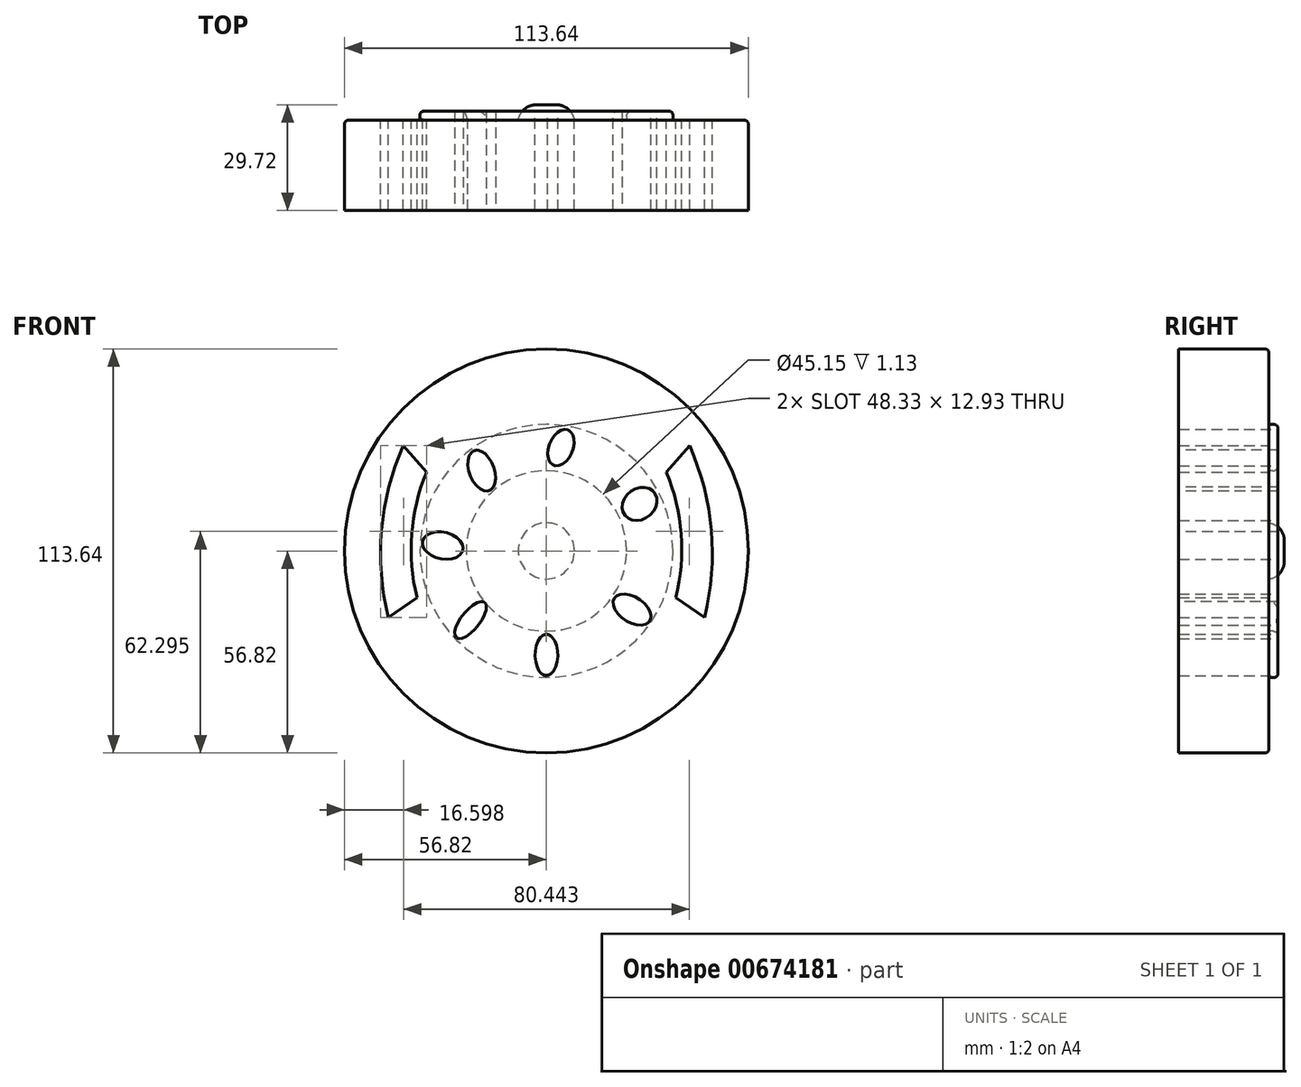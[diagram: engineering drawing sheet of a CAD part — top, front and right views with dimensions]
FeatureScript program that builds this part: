
annotation { "Feature Type Name" : "Feature", "Feature Type Description" : "" }
export const myFeature = defineFeature(function(context is Context, id is Id, definition is map)
    precondition{}
    {
        {
            var Q0;
            Q0=qCreatedBy(makeId("Front.planeOp"),FACE);
            var sketch = newSketch(context, id + "F0", { "sketchPlane" : qUnion([Q0])});
            skCircle(sketch, "E0", {"center": v(0, 0) * mm, "radius": 56.82 * mm});
            skSolve(sketch);
        }
        {
            var Q0;
            Q0=makeQuery(id+"F0.imprint","IMPRINT",FACE,{"disambiguationData":[TD([[makeQuery(id+"F0.imprint","IMPRINT",EDGE,{"derivedFrom":sQuery(id+"F0.wireOp",EDGE,"E0")}),1.0]])]});
            var sketch = newSketch(context, id + "F1", { "sketchPlane" : qUnion([Q0])});
            skLineSegment(sketch, "E1", {"start": v(0, 72.6) * mm, "end": v(0, -72.88) * mm, "construction": true});
            skLineSegment(sketch, "E2", {"start": v(-75.95, 0) * mm, "end": v(77.07, 0) * mm, "construction": true});
            skLineSegment(sketch, "E3", {"start": v(-40.28, 29.64) * mm, "end": v(-33.76, 22.16) * mm});
            skLineSegment(sketch, "E4", {"start": v(-44.47, -18.7) * mm, "end": v(-36.41, -13.13) * mm});
            skArc(sketch, "E5", {"start": v(-40.28, 29.64) * mm, "mid": v(-46.4, 5.82) * mm, "end": v(-44.47, -18.7) * mm});
            skArc(sketch, "E6", {"start": v(-33.76, 22.16) * mm, "mid": v(-37.9, 4.73) * mm, "end": v(-36.41, -13.13) * mm});
            skArc(sketch, "E7.MirrorCS", {"start": v(33.76, 22.16) * mm, "mid": v(37.9, 4.73) * mm, "end": v(36.41, -13.13) * mm});
            skLineSegment(sketch, "E8.MirrorCS", {"start": v(40.28, 29.64) * mm, "end": v(33.76, 22.16) * mm});
            skArc(sketch, "E9.MirrorCS", {"start": v(40.28, 29.64) * mm, "mid": v(46.4, 5.82) * mm, "end": v(44.47, -18.7) * mm});
            skLineSegment(sketch, "E10.MirrorCS", {"start": v(44.47, -18.7) * mm, "end": v(36.41, -13.13) * mm});
            skSolve(sketch);
        }
        {
            var Q0;
            Q0=makeQuery(id+"F1.imprint","IMPRINT",FACE,{"disambiguationData":[TD([[makeQuery(id+"F1.imprint","IMPRINT",EDGE,{"derivedFrom":sQuery(id+"F1.wireOp",EDGE,"E3")}),1.0]])]});
            extrude(context, id + "F2", {"entities" : qUnion([Q0]), "depth" : 25.4 * mm, "offsetDistance" : 25.4 * mm});
        }
        {
            var Q0;
            Q0=makeQuery(id+"F0.imprint","IMPRINT",FACE,{"disambiguationData":[TD([[makeQuery(id+"F0.imprint","IMPRINT",EDGE,{"derivedFrom":sQuery(id+"F0.wireOp",EDGE,"E0")}),1.0]])]});
            var sketch = newSketch(context, id + "F3", { "sketchPlane" : qUnion([Q0])});
            skCircle(sketch, "E11", {"center": v(0, 0) * mm, "radius": 35.59 * mm});
            skCircle(sketch, "E12", {"center": v(0, 0) * mm, "radius": 22.58 * mm});
            skSolve(sketch);
        }
        {
            var Q0;
            Q0 = qSketchRegion(id + "F3", true);
            var Q1;
            Q1=makeQuery(id+"F2.opExtrude","CAP_FACE",FACE,{"disambiguationData":[OSD([sQuery(id+"F0.wireOp",EDGE,"E0"),sQuery(id+"F1.wireOp",EDGE,"E3"),sQuery(id+"F1.wireOp",EDGE,"E4"),sQuery(id+"F1.wireOp",EDGE,"E5"),sQuery(id+"F1.wireOp",EDGE,"E6"),sQuery(id+"F1.wireOp",EDGE,"E7.MirrorCS"),sQuery(id+"F1.wireOp",EDGE,"E8.MirrorCS"),sQuery(id+"F1.wireOp",EDGE,"E9.MirrorCS"),sQuery(id+"F1.wireOp",EDGE,"E10.MirrorCS")])],"isStart":false});
            extrude(context, id + "F4", {"entities" : qUnion([Q0, Q1]), "operationType" : NewBodyOperationType.ADD, "oppositeDirection" : true, "depth" : 2.54 * mm, "offsetDistance" : 25.4 * mm});
        }
        {
            var Q0;
            Q0=makeQuery(id+"F4.opExtrude","CAP_FACE",FACE,{"disambiguationData":[OSD([sQuery(id+"F3.wireOp",EDGE,"E11"),sQuery(id+"F3.wireOp",EDGE,"E12")])],"isStart":false});
            var sketch = newSketch(context, id + "F5", { "sketchPlane" : qUnion([Q0])});
            skEllipse(sketch, "E13", {"center": v(-26.2, 13.23) * mm, "majorRadius": 5.24 * mm, "minorRadius": 4.3 * mm, "majorAxis": v(0.78, -0.63)});
            skEllipse(sketch, "E14", {"center": v(-4.1, 29.07) * mm, "majorRadius": 5.36 * mm, "minorRadius": 3.4 * mm, "majorAxis": v(-0.37, 0.93)});
            skEllipse(sketch, "E15", {"center": v(18.2, 22.6) * mm, "majorRadius": 6 * mm, "minorRadius": 3.5 * mm, "majorAxis": v(0.35, 0.93)});
            skEllipse(sketch, "E16", {"center": v(29.17, 1.5) * mm, "majorRadius": 5.8 * mm, "minorRadius": 3.78 * mm, "majorAxis": v(0.98, 0.21)});
            skEllipse(sketch, "E17", {"center": v(-24.1, -16.5) * mm, "majorRadius": 5.94 * mm, "minorRadius": 3.55 * mm, "majorAxis": v(0.84, 0.54)});
            skEllipse(sketch, "E18", {"center": v(0, -29.27) * mm, "majorRadius": 5.81 * mm, "minorRadius": 3.2 * mm, "majorAxis": v(0, 1)});
            skEllipse(sketch, "E19", {"center": v(21.33, -19.45) * mm, "majorRadius": 6.35 * mm, "minorRadius": 2.59 * mm, "majorAxis": v(0.62, -0.78)});
            skSolve(sketch);
        }
        {
            var Q0;
            Q0=makeQuery(id+"F5.imprint","IMPRINT",FACE,{"disambiguationData":[TD([[makeQuery(id+"F5.imprint","IMPRINT",EDGE,{"derivedFrom":sQuery(id+"F5.wireOp",EDGE,"E13")}),1.0]])]});
            var Q1;
            Q1=makeQuery(id+"F5.imprint","IMPRINT",FACE,{"disambiguationData":[TD([[makeQuery(id+"F5.imprint","IMPRINT",EDGE,{"derivedFrom":sQuery(id+"F5.wireOp",EDGE,"E17")}),1.0]])]});
            var Q2;
            Q2=makeQuery(id+"F5.imprint","IMPRINT",FACE,{"disambiguationData":[TD([[makeQuery(id+"F5.imprint","IMPRINT",EDGE,{"derivedFrom":sQuery(id+"F5.wireOp",EDGE,"E18")}),1.0]])]});
            var Q3;
            Q3=makeQuery(id+"F5.imprint","IMPRINT",FACE,{"disambiguationData":[TD([[makeQuery(id+"F5.imprint","IMPRINT",EDGE,{"derivedFrom":sQuery(id+"F5.wireOp",EDGE,"E19")}),1.0]])]});
            var Q4;
            Q4=makeQuery(id+"F5.imprint","IMPRINT",FACE,{"disambiguationData":[TD([[makeQuery(id+"F5.imprint","IMPRINT",EDGE,{"derivedFrom":sQuery(id+"F5.wireOp",EDGE,"E16")}),1.0]])]});
            var Q5;
            Q5=makeQuery(id+"F5.imprint","IMPRINT",FACE,{"disambiguationData":[TD([[makeQuery(id+"F5.imprint","IMPRINT",EDGE,{"derivedFrom":sQuery(id+"F5.wireOp",EDGE,"E14")}),1.0]])]});
            var Q6;
            Q6=makeQuery(id+"F5.imprint","IMPRINT",FACE,{"disambiguationData":[TD([[makeQuery(id+"F5.imprint","IMPRINT",EDGE,{"derivedFrom":sQuery(id+"F5.wireOp",EDGE,"E15")}),1.0]])]});
            extrude(context, id + "F6", {"entities" : qUnion([Q0, Q1, Q2, Q3, Q4, Q5, Q6]), "operationType" : NewBodyOperationType.REMOVE, "endBound" : BoundingType.UP_TO_NEXT, "oppositeDirection" : true, "depth" : 0.25 * mm, "offsetDistance" : 25.4 * mm});
        }
        {
            var Q0;
            Q0=makeQuery(id+"F0.imprint","IMPRINT",FACE,{"disambiguationData":[TD([[makeQuery(id+"F0.imprint","IMPRINT",EDGE,{"derivedFrom":sQuery(id+"F0.wireOp",EDGE,"E0")}),1.0]])]});
            var sketch = newSketch(context, id + "F7", { "sketchPlane" : qUnion([Q0])});
            skCircle(sketch, "E20", {"center": v(0, 0) * mm, "radius": 7.9 * mm});
            skSolve(sketch);
        }
        {
            var Q0;
            Q0=makeQuery(id+"F7.imprint","IMPRINT",FACE,{"disambiguationData":[TD([[makeQuery(id+"F7.imprint","IMPRINT",EDGE,{"derivedFrom":sQuery(id+"F7.wireOp",EDGE,"E20")}),1.0]])]});
            extrude(context, id + "F8", {"entities" : qUnion([Q0]), "operationType" : NewBodyOperationType.ADD, "oppositeDirection" : true, "depth" : 4.32 * mm, "offsetDistance" : 25.4 * mm});
        }
        {
            var Q0;
            Q0=makeQuery(id+"F8.opExtrude","CAP_EDGE",EDGE,{"disambiguationData":[OSD([sQuery(id+"F7.wireOp",EDGE,"E20")])],"isStart":false});
            fillet(context, id + "F9", {"entities" : qUnion([Q0]), "radius" : 5.08 * mm, "tangentPropagation" : true, "allowEdgeOverflow" : false});
        }
        {
            var Q0;
            Q0=makeQuery(id+"F4.opExtrude","CAP_EDGE",EDGE,{"disambiguationData":[OSD([sQuery(id+"F3.wireOp",EDGE,"E12")])],"isStart":false});
            fillet(context, id + "F10", {"entities" : qUnion([Q0]), "radius" : 1.41 * mm, "tangentPropagation" : true, "allowEdgeOverflow" : false});
        }
        {
            var Q0;
            Q0=makeQuery(id+"F4.opExtrude","CAP_EDGE",EDGE,{"disambiguationData":[OSD([sQuery(id+"F3.wireOp",EDGE,"E11")])],"isStart":false});
            fillet(context, id + "F11", {"entities" : qUnion([Q0]), "radius" : 1.1 * mm, "tangentPropagation" : true, "allowEdgeOverflow" : false});
        }
        {
            var Q0;
            Q0=makeQuery(id+"F2.opExtrude","CAP_EDGE",EDGE,{"disambiguationData":[OSD([sQuery(id+"F0.wireOp",EDGE,"E0")])],"isStart":true});
            fillet(context, id + "F12", {"entities" : qUnion([Q0]), "radius" : 1.1 * mm, "tangentPropagation" : true, "allowEdgeOverflow" : false});
        }
    });
